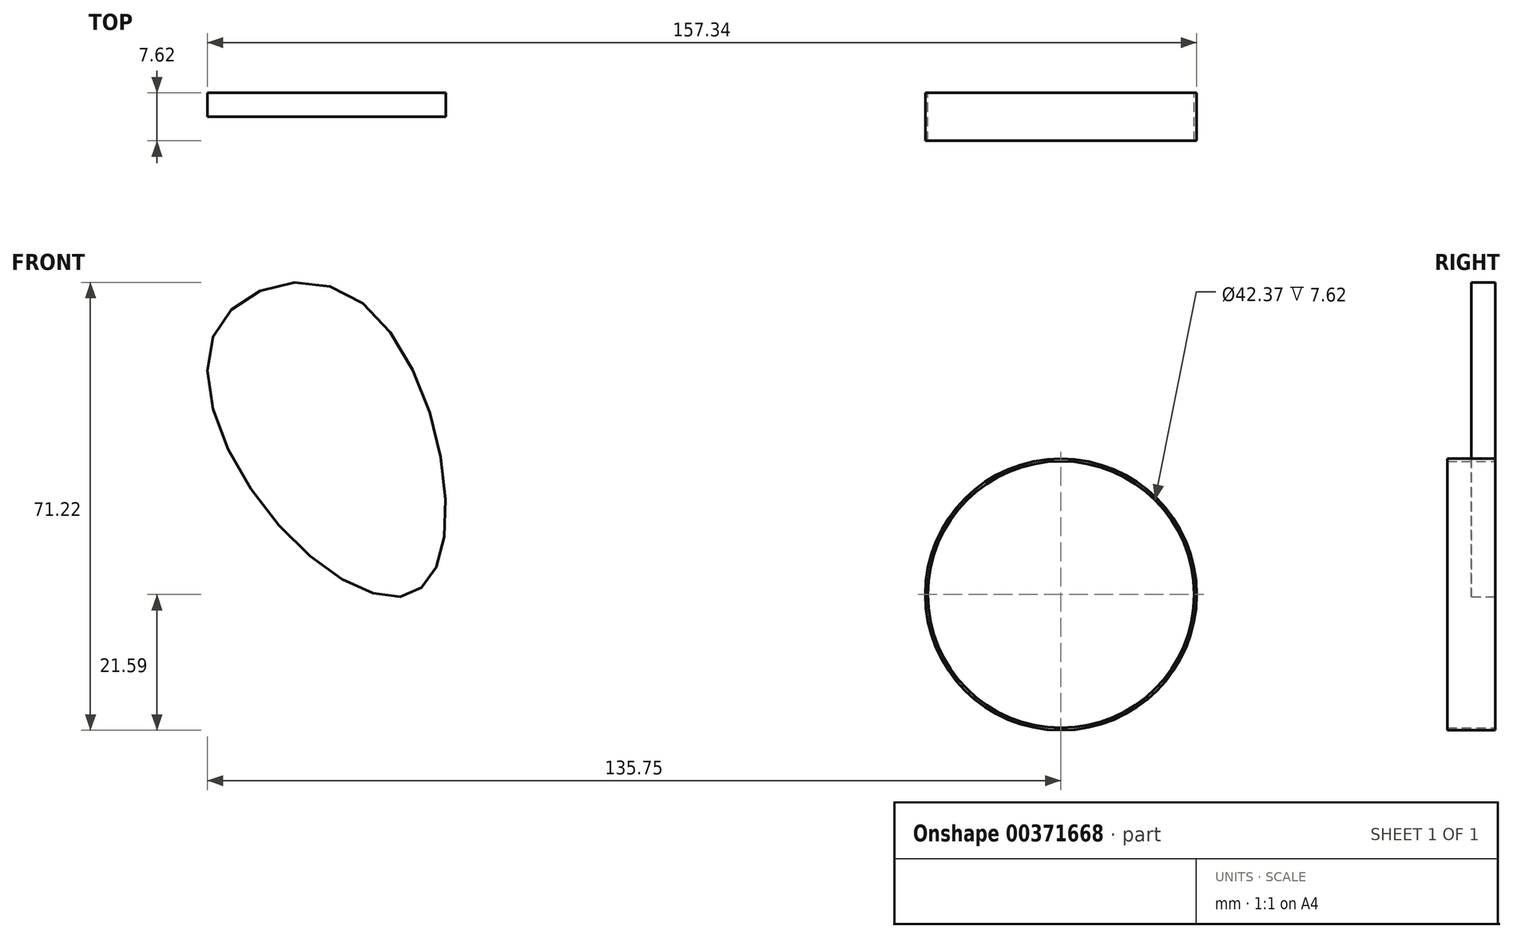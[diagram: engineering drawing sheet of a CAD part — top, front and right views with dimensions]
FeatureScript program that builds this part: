
annotation { "Feature Type Name" : "Feature", "Feature Type Description" : "" }
export const myFeature = defineFeature(function(context is Context, id is Id, definition is map)
    precondition{}
    {
        {
            var Q0;
            Q0=qCreatedBy(makeId("Front.planeOp"),FACE);
            var sketch = newSketch(context, id + "F0", { "sketchPlane" : qUnion([Q0])});
            skCircle(sketch, "E0", {"center": v(0, 0) * mm, "radius": 21.59 * mm});
            skCircle(sketch, "E1", {"center": v(0, 0) * mm, "radius": 21.15 * mm});
            skCircle(sketch, "E2", {"center": v(0, 0) * mm, "radius": 20.32 * mm});
            skCircle(sketch, "E3", {"center": v(0, 0) * mm, "radius": 21.18 * mm});
            skSolve(sketch);
        }
        {
            var Q0;
            Q0 = qSketchRegion(id + "F0", true);
            extrude(context, id + "F1", {"entities" : qUnion([Q0]), "depth" : 7.62 * mm});
        }
        {
            var Q0;
            Q0=qCreatedBy(makeId("Front.planeOp"),FACE);
            var sketch = newSketch(context, id + "F2", { "sketchPlane" : qUnion([Q0])});
            skFitSpline(sketch, "E4", {"points": [v(-124.36, 11.03) * mm, v(-134.49, 41.85) * mm, v(-114.24, 48.26) * mm, v(-97.93, 16.4) * mm, v(-103.55, 0) * mm, v(-124.36, 11.03) * mm]});
            skSolve(sketch);
        }
        {
            var Q0;
            Q0 = qSketchRegion(id + "F2", true);
            extrude(context, id + "F3", {"entities" : qUnion([Q0]), "depth" : 3.8 * mm});
        }
    });
